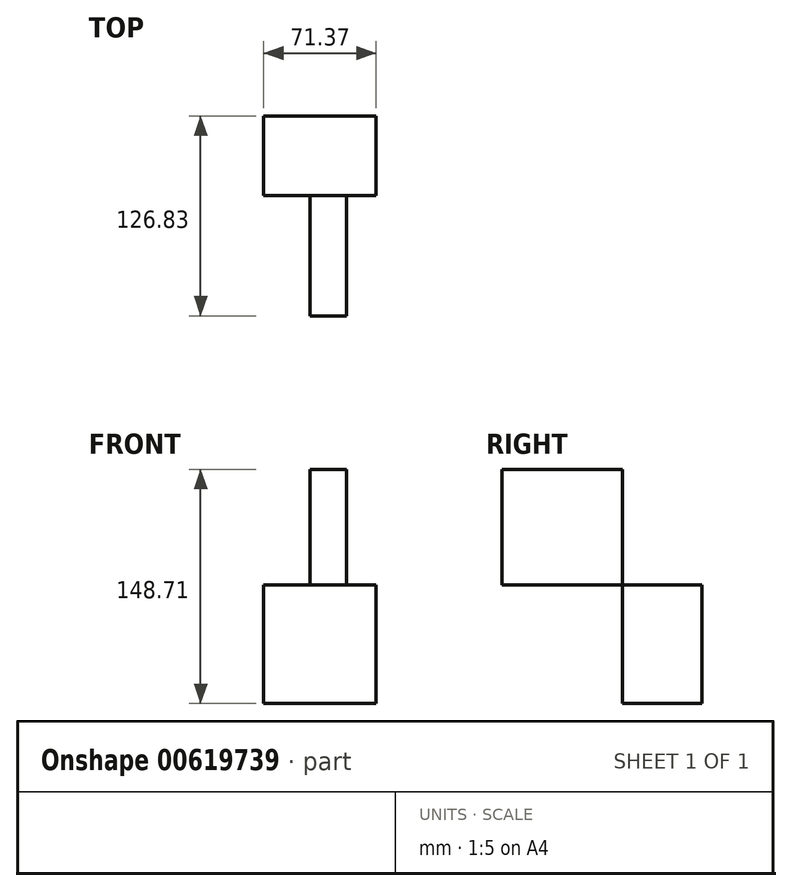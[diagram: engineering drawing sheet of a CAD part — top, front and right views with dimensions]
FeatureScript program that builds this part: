
annotation { "Feature Type Name" : "Feature", "Feature Type Description" : "" }
export const myFeature = defineFeature(function(context is Context, id is Id, definition is map)
    precondition{}
    {
        {
            var Q0;
            Q0=qCreatedBy(makeId("Right.planeOp"),FACE);
            var sketch = newSketch(context, id + "F0", { "sketchPlane" : qUnion([Q0])});
            skLineSegment(sketch, "E0.bottom", {"start": v(0, 0) * mm, "end": v(-50.38, 0) * mm});
            skLineSegment(sketch, "E0.top", {"start": v(0, 75.38) * mm, "end": v(-50.38, 75.38) * mm});
            skLineSegment(sketch, "E0.left", {"start": v(0, 0) * mm, "end": v(0, 75.38) * mm});
            skLineSegment(sketch, "E0.right", {"start": v(-50.38, 0) * mm, "end": v(-50.38, 75.38) * mm});
            skSolve(sketch);
        }
        {
            var Q0;
            Q0=makeQuery(id+"F0.imprint","IMPRINT",FACE,{"disambiguationData":[TD([[makeQuery(id+"F0.imprint","IMPRINT",EDGE,{"derivedFrom":sQuery(id+"F0.wireOp",EDGE,"E0.bottom")}),-1.0]])]});
            extrude(context, id + "F1", {"entities" : qUnion([Q0]), "depth" : 71.37 * mm, "offsetDistance" : 25.4 * mm});
        }
        {
            var Q0;
            Q0=makeQuery(id+"F1.opExtrude","SWEPT_FACE",FACE,{"disambiguationData":[OSD([sQuery(id+"F0.wireOp",EDGE,"E0.right")])]});
            var sketch = newSketch(context, id + "F2", { "sketchPlane" : qUnion([Q0])});
            skLineSegment(sketch, "E1.bottom", {"start": v(29.34, 34.95) * mm, "end": v(52.5, 34.95) * mm});
            skLineSegment(sketch, "E1.top", {"start": v(29.34, 148.71) * mm, "end": v(52.5, 148.71) * mm});
            skLineSegment(sketch, "E1.left", {"start": v(29.34, 34.95) * mm, "end": v(29.34, 148.71) * mm});
            skLineSegment(sketch, "E1.right", {"start": v(52.5, 34.95) * mm, "end": v(52.5, 148.71) * mm});
            skSolve(sketch);
        }
        {
            var Q0;
            {var subQ0=sQuery(id+"F2.wireOp",EDGE,"E1.top");Q0=makeQuery(id+"F2.imprint","IMPRINT",FACE,{"disambiguationData":[TD([[makeQuery(id+"F2.imprint","IMPRINT",EDGE,{"derivedFrom":subQ0}),-1.0]])]});}
            extrude(context, id + "F3", {"entities" : qUnion([Q0]), "depth" : 76.45 * mm, "offsetDistance" : 25.4 * mm});
        }
    });
